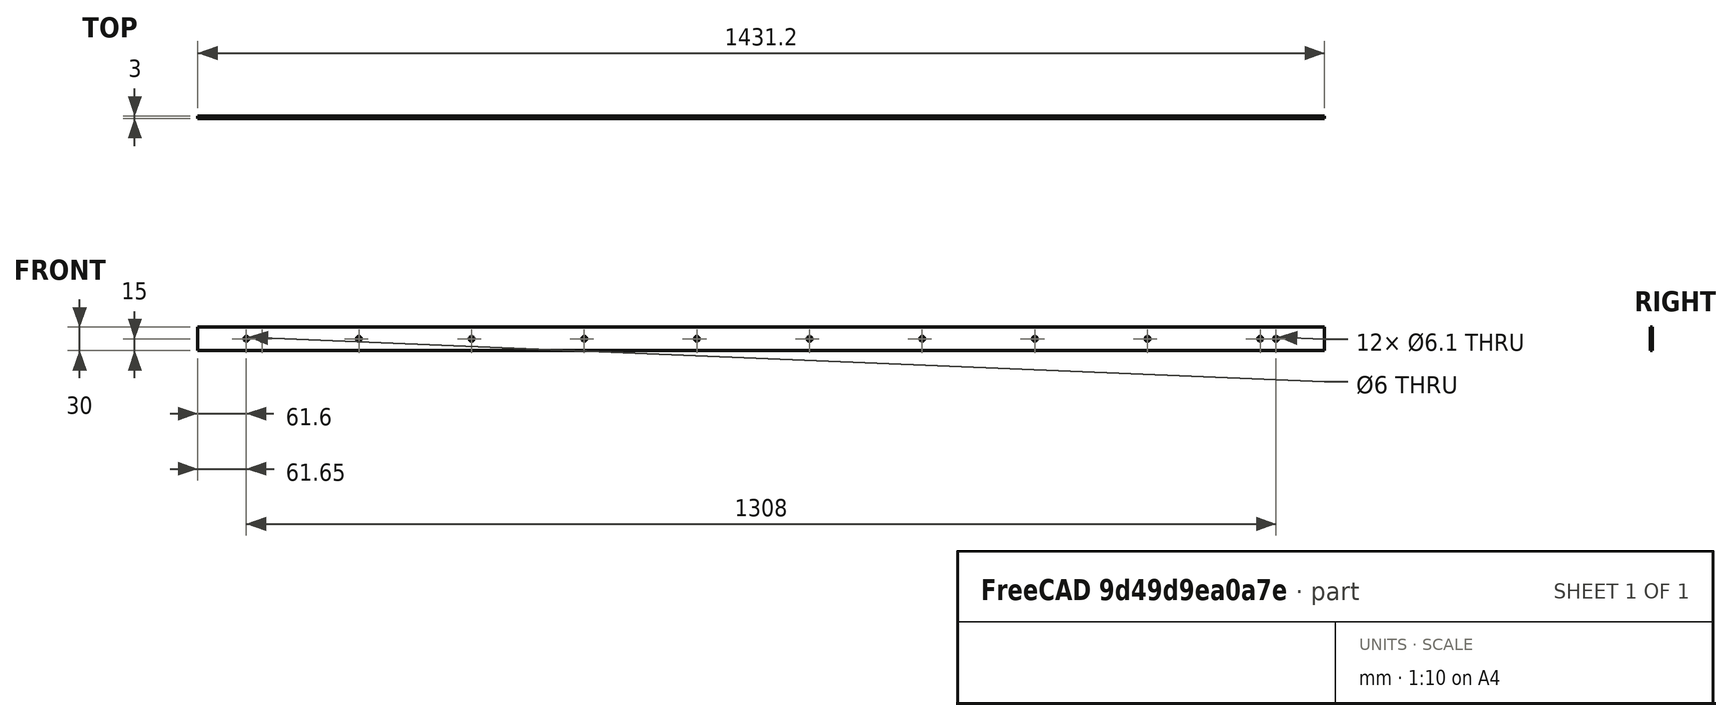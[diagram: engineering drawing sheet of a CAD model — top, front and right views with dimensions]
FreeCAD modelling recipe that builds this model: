
FCSTD DOCUMENT  (FreeCAD 0.15R4671 (Git))
Label: gabarit super critique
License: All rights reserved
LicenseURL: http://en.wikipedia.org/wiki/All_rights_reserved
objects: Sketcher::SketchObject×1, PartDesign::Pad×1
note: 3 computed .brp shape members not serialized (recipe doc carries the construction recipe); baked Part::Feature solids carry a one-line shape summary decoded from their .brp

FEATURE [Sketcher::SketchObject] Sketch
  Placement = pos=(0,0,0) rot=(1,0,0;1.5708rad)
  sketch-geometry (18):
    g0: Circle CenterX=-10.05 CenterY=0 CenterZ=0 NormalX=0 NormalY=0 NormalZ=1 Radius=3.05
    g1: Circle CenterX=10.05 CenterY=0 CenterZ=0 NormalX=0 NormalY=0 NormalZ=1 Radius=3.05
    g2: LineSegment StartX=-71.65 StartY=15 StartZ=0 EndX=1359.65 EndY=15 EndZ=0
    g3: LineSegment StartX=1359.65 StartY=15 StartZ=0 EndX=1359.65 EndY=-15 EndZ=0
    g4: LineSegment StartX=1359.65 StartY=-15 StartZ=0 EndX=-71.65 EndY=-15 EndZ=0
    g5: LineSegment StartX=-71.65 StartY=-15 StartZ=0 EndX=-71.65 EndY=15 EndZ=0
    g6: Circle CenterX=133.15 CenterY=0 CenterZ=0 NormalX=0 NormalY=0 NormalZ=1 Radius=3.05
    g7: Circle CenterX=276.25 CenterY=0 CenterZ=0 NormalX=0 NormalY=0 NormalZ=1 Radius=3.05
    g8: Circle CenterX=419.35 CenterY=0 CenterZ=0 NormalX=0 NormalY=0 NormalZ=1 Radius=3.05
    g9: Circle CenterX=562.45 CenterY=0 CenterZ=0 NormalX=0 NormalY=0 NormalZ=1 Radius=3.05
    g10: Circle CenterX=705.55 CenterY=0 CenterZ=0 NormalX=0 NormalY=0 NormalZ=1 Radius=3.05
    g11: Circle CenterX=848.65 CenterY=0 CenterZ=0 NormalX=0 NormalY=0 NormalZ=1 Radius=3.05
    g12: Circle CenterX=991.75 CenterY=0 CenterZ=0 NormalX=0 NormalY=0 NormalZ=1 Radius=3.05
    g13: Circle CenterX=1134.85 CenterY=0 CenterZ=0 NormalX=0 NormalY=0 NormalZ=1 Radius=3.05
    g14: Circle CenterX=1277.95 CenterY=0 CenterZ=0 NormalX=0 NormalY=0 NormalZ=1 Radius=3.05
    g15: Circle CenterX=1298.05 CenterY=0 CenterZ=0 NormalX=0 NormalY=0 NormalZ=1 Radius=3.05
    g16: Circle CenterX=-10 CenterY=0 CenterZ=0 NormalX=0 NormalY=0 NormalZ=1 Radius=3
    g17: Circle CenterX=-9.95 CenterY=0 CenterZ=0 NormalX=0 NormalY=0 NormalZ=1 Radius=3.05
  constraints (55):
    c: PointOnObject(g0,g-1)
    c: PointOnObject(g1,g-1)
    c: Symmetric(g0,g1,g-2)
    c: DistanceX(g0,g1) = 20.1
    c: Coincident(g2,g3)
    c: Coincident(g3,g4)
    c: Coincident(g4,g5)
    c: Coincident(g5,g2)
    c: Horizontal(g2)
    c: Horizontal(g4)
    c: Vertical(g3)
    c: Vertical(g5)
    c: DistanceY(g5) = 30
    c: Symmetric(g2,g4,g-1)
    c: PointOnObject(g6,g-1)
    c: Radius(g0) = 3.05
    c: Equal(g0,g1)
    c: Equal(g0,g6)
    c: DistanceX(g2,g0) = 61.6
    c: PointOnObject(g7,g-1)
    c: PointOnObject(g8,g-1)
    c: PointOnObject(g9,g-1)
    c: PointOnObject(g10,g-1)
    c: PointOnObject(g11,g-1)
    c: PointOnObject(g12,g-1)
    c: PointOnObject(g13,g-1)
    c: PointOnObject(g14,g-1)
    c: PointOnObject(g15,g-1)
    c: Equal(g0,g7)
    c: Equal(g7,g8)
    c: Equal(g8,g9)
    c: Equal(g9,g10)
    c: Equal(g10,g11)
    c: Equal(g11,g13)
    c: Equal(g13,g12)
    c: Equal(g12,g14)
    c: Equal(g14,g15)
    c: DistanceX(g15,g2) = 61.6
    c: DistanceX(g14,g15) = 20.1
    c: DistanceX(g14,g13) = -143.1
    c: DistanceX(g12,g13) = 143.1
    c: DistanceX(g11,g12) = 143.1
    c: DistanceX(g10,g11) = 143.1
    c: DistanceX(g9,g10) = 143.1
    c: DistanceX(g8,g9) = 143.1
    c: DistanceX(g7,g8) = 143.1
    c: DistanceX(g6,g7) = 143.1
    c: PointOnObject(g16,g-1)
    c: Radius(g16) = 3
    c: Tangent(g16,g0)
    c: PointOnObject(g17,g-1)
    c: Radius(g17) = 3.05
    c: Tangent(g17,g16)
    c: DistanceX(g17,g6) = 143.1
    c: DistanceX(g4,g15) = 1369.7
FEATURE [PartDesign::Pad] Pad
  Length = 3
  Length2 = 100
  Placement = pos=(0,0,0) rot=(1,0,0;1.5708rad)
  Sketch = -> Sketch
  Type = 0
